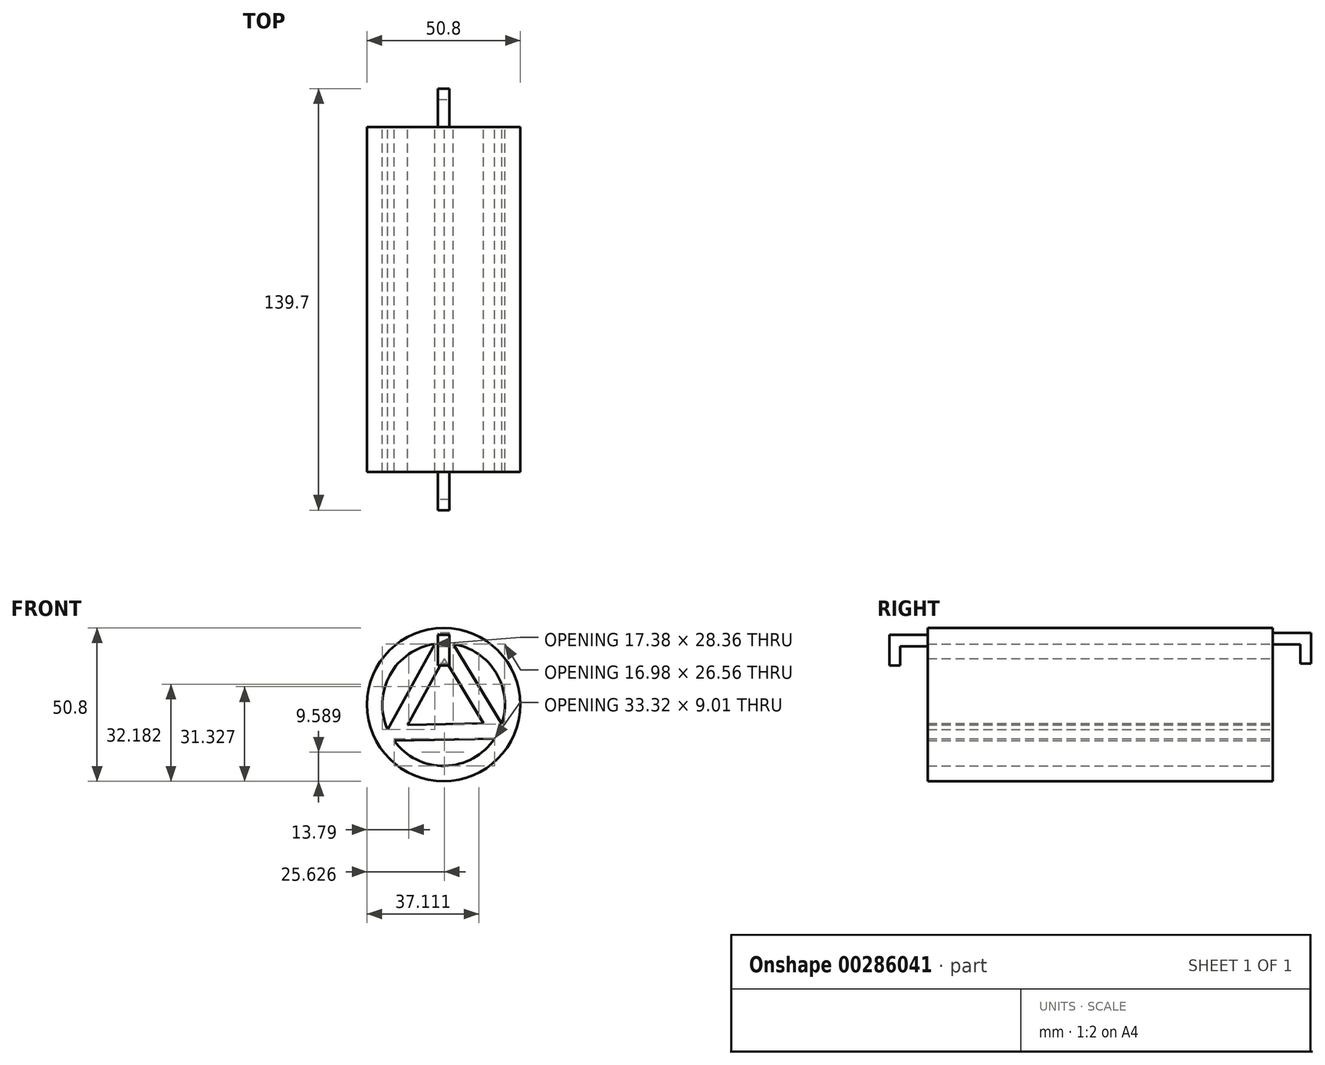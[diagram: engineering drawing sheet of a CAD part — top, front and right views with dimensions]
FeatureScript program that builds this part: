
annotation { "Feature Type Name" : "Feature", "Feature Type Description" : "" }
export const myFeature = defineFeature(function(context is Context, id is Id, definition is map)
    precondition{}
    {
        {
            var Q0;
            Q0=qCreatedBy(makeId("Front.planeOp"),FACE);
            var sketch = newSketch(context, id + "F0", { "sketchPlane" : qUnion([Q0])});
            skArc(sketch, "E0", {"start": v(-2.92, 20.1) * mm, "mid": v(-17.8, 9.82) * mm, "end": v(-18.57, -8.25) * mm});
            skCircle(sketch, "E1", {"center": v(0, 0) * mm, "radius": 25.4 * mm});
            skLineSegment(sketch, "E2", {"start": v(-2.92, 20.1) * mm, "end": v(-18.57, -8.25) * mm});
            skLineSegment(sketch, "E3", {"start": v(-16.43, -11.95) * mm, "end": v(16.88, -11.3) * mm});
            skLineSegment(sketch, "E4", {"start": v(19.25, -6.5) * mm, "end": v(3.22, 20.06) * mm});
            skLineSegment(sketch, "E5.0", {"start": v(13.2, -6.3) * mm, "end": v(0.2, 15.24) * mm});
            skLineSegment(sketch, "E5.1", {"start": v(-11.96, -6.78) * mm, "end": v(13.2, -6.3) * mm});
            skLineSegment(sketch, "E5.2", {"start": v(0.2, 15.24) * mm, "end": v(-11.96, -6.78) * mm});
            skPoint(sketch, "E6.orphan", {"position": v(0, 25.4) * mm});
            skArc(sketch, "E7.trimOffspring", {"start": v(-16.43, -11.95) * mm, "mid": v(0.4, -20.32) * mm, "end": v(16.88, -11.3) * mm});
            skArc(sketch, "E8.trimOffspring", {"start": v(19.25, -6.5) * mm, "mid": v(17.4, 10.5) * mm, "end": v(3.22, 20.06) * mm});
            skSolve(sketch);
        }
        {
            var Q0;
            Q0 = qSketchRegion(id + "F0", true);
            extrude(context, id + "F1", {"entities" : qUnion([Q0]), "depth" : 114.3 * mm});
        }
        {
            var Q0;
            Q0=makeQuery(id+"F1.opExtrude","CAP_FACE",FACE,{"disambiguationData":[OSD([sQuery(id+"F0.wireOp",EDGE,"E0"),sQuery(id+"F0.wireOp",EDGE,"E1"),sQuery(id+"F0.wireOp",EDGE,"E2"),sQuery(id+"F0.wireOp",EDGE,"E3"),sQuery(id+"F0.wireOp",EDGE,"E4"),sQuery(id+"F0.wireOp",EDGE,"E5.0"),sQuery(id+"F0.wireOp",EDGE,"E5.1"),sQuery(id+"F0.wireOp",EDGE,"E5.2"),sQuery(id+"F0.wireOp",EDGE,"E7.trimOffspring"),sQuery(id+"F0.wireOp",EDGE,"E8.trimOffspring")])],"isStart":true});
            var sketch = newSketch(context, id + "F2", { "sketchPlane" : qUnion([Q0])});
            skLineSegment(sketch, "E9.bottom", {"start": v(-1.9, 23.8) * mm, "end": v(1.9, 23.8) * mm});
            skLineSegment(sketch, "E9.top", {"start": v(-1.9, 19.99) * mm, "end": v(1.9, 19.99) * mm});
            skLineSegment(sketch, "E9.left", {"start": v(-1.9, 23.8) * mm, "end": v(-1.9, 19.99) * mm});
            skLineSegment(sketch, "E9.right", {"start": v(1.9, 23.8) * mm, "end": v(1.9, 19.99) * mm});
            skPoint(sketch, "E9.middle", {"position": v(0, 21.9) * mm});
            skSolve(sketch);
        }
        {
            var Q0;
            Q0 = qSketchRegion(id + "F2", true);
            extrude(context, id + "F3", {"entities" : qUnion([Q0]), "operationType" : NewBodyOperationType.ADD, "depth" : 12.7 * mm});
        }
        {
            var Q0;
            Q0=makeQuery(id+"F1.opExtrude","CAP_FACE",FACE,{"disambiguationData":[OSD([sQuery(id+"F0.wireOp",EDGE,"E0"),sQuery(id+"F0.wireOp",EDGE,"E1"),sQuery(id+"F0.wireOp",EDGE,"E2"),sQuery(id+"F0.wireOp",EDGE,"E3"),sQuery(id+"F0.wireOp",EDGE,"E4"),sQuery(id+"F0.wireOp",EDGE,"E5.0"),sQuery(id+"F0.wireOp",EDGE,"E5.1"),sQuery(id+"F0.wireOp",EDGE,"E5.2"),sQuery(id+"F0.wireOp",EDGE,"E7.trimOffspring"),sQuery(id+"F0.wireOp",EDGE,"E8.trimOffspring")])],"isStart":false});
            var sketch = newSketch(context, id + "F4", { "sketchPlane" : qUnion([Q0])});
            skLineSegment(sketch, "E10.bottom", {"start": v(-1.9, 23.09) * mm, "end": v(1.9, 23.09) * mm});
            skLineSegment(sketch, "E10.top", {"start": v(-1.9, 19.28) * mm, "end": v(1.9, 19.28) * mm});
            skLineSegment(sketch, "E10.left", {"start": v(-1.9, 23.09) * mm, "end": v(-1.9, 19.28) * mm});
            skLineSegment(sketch, "E10.right", {"start": v(1.9, 23.09) * mm, "end": v(1.9, 19.28) * mm});
            skPoint(sketch, "E10.middle", {"position": v(0, 21.18) * mm});
            skSolve(sketch);
        }
        {
            var Q0;
            Q0=makeQuery(id+"F4.imprint","IMPRINT",FACE,{"disambiguationData":[TD([[makeQuery(id+"F4.imprint","IMPRINT",EDGE,{"derivedFrom":sQuery(id+"F4.wireOp",EDGE,"E10.bottom")}),-1.0]])]});
            extrude(context, id + "F5", {"entities" : qUnion([Q0]), "operationType" : NewBodyOperationType.ADD, "depth" : 12.7 * mm});
        }
        {
            var Q0;
            Q0=makeQuery(id+"F3.opExtrude","SWEPT_FACE",FACE,{"disambiguationData":[OSD([sQuery(id+"F2.wireOp",EDGE,"E9.top")])]});
            var sketch = newSketch(context, id + "F6", { "sketchPlane" : qUnion([Q0])});
            skLineSegment(sketch, "E11", {"start": v(-1.9, -9.14) * mm, "end": v(1.9, -9.14) * mm});
            skSolve(sketch);
        }
        {
            var Q0;
            Q0 = qSketchRegion(id + "F6", true);
            var Q1;
            {var subQ0=sQuery(id+"F6.wireOp",EDGE,"E11");Q1=makeQuery(id+"F6.imprint","IMPRINT",FACE,{"disambiguationData":[TD([[makeQuery(id+"F6.imprint","IMPRINT",EDGE,{"derivedFrom":subQ0}),-1.0]])]});}
            extrude(context, id + "F7", {"entities" : qUnion([Q0, Q1]), "operationType" : NewBodyOperationType.ADD, "depth" : 6.35 * mm});
        }
        {
            var Q0;
            Q0=makeQuery(id+"F5.opExtrude","SWEPT_FACE",FACE,{"disambiguationData":[OSD([sQuery(id+"F4.wireOp",EDGE,"E10.top")])]});
            var sketch = newSketch(context, id + "F8", { "sketchPlane" : qUnion([Q0])});
            skLineSegment(sketch, "E12", {"start": v(1.9, 123.44) * mm, "end": v(-1.9, 123.44) * mm});
            skSolve(sketch);
        }
        {
            var Q0;
            Q0 = qSketchRegion(id + "F8", true);
            var Q1;
            {var subQ0=sQuery(id+"F8.wireOp",EDGE,"E12");Q1=makeQuery(id+"F8.imprint","IMPRINT",FACE,{"disambiguationData":[TD([[makeQuery(id+"F8.imprint","IMPRINT",EDGE,{"derivedFrom":subQ0}),-1.0]])]});}
            extrude(context, id + "F9", {"entities" : qUnion([Q0, Q1]), "operationType" : NewBodyOperationType.ADD, "depth" : 6.35 * mm});
        }
    });
